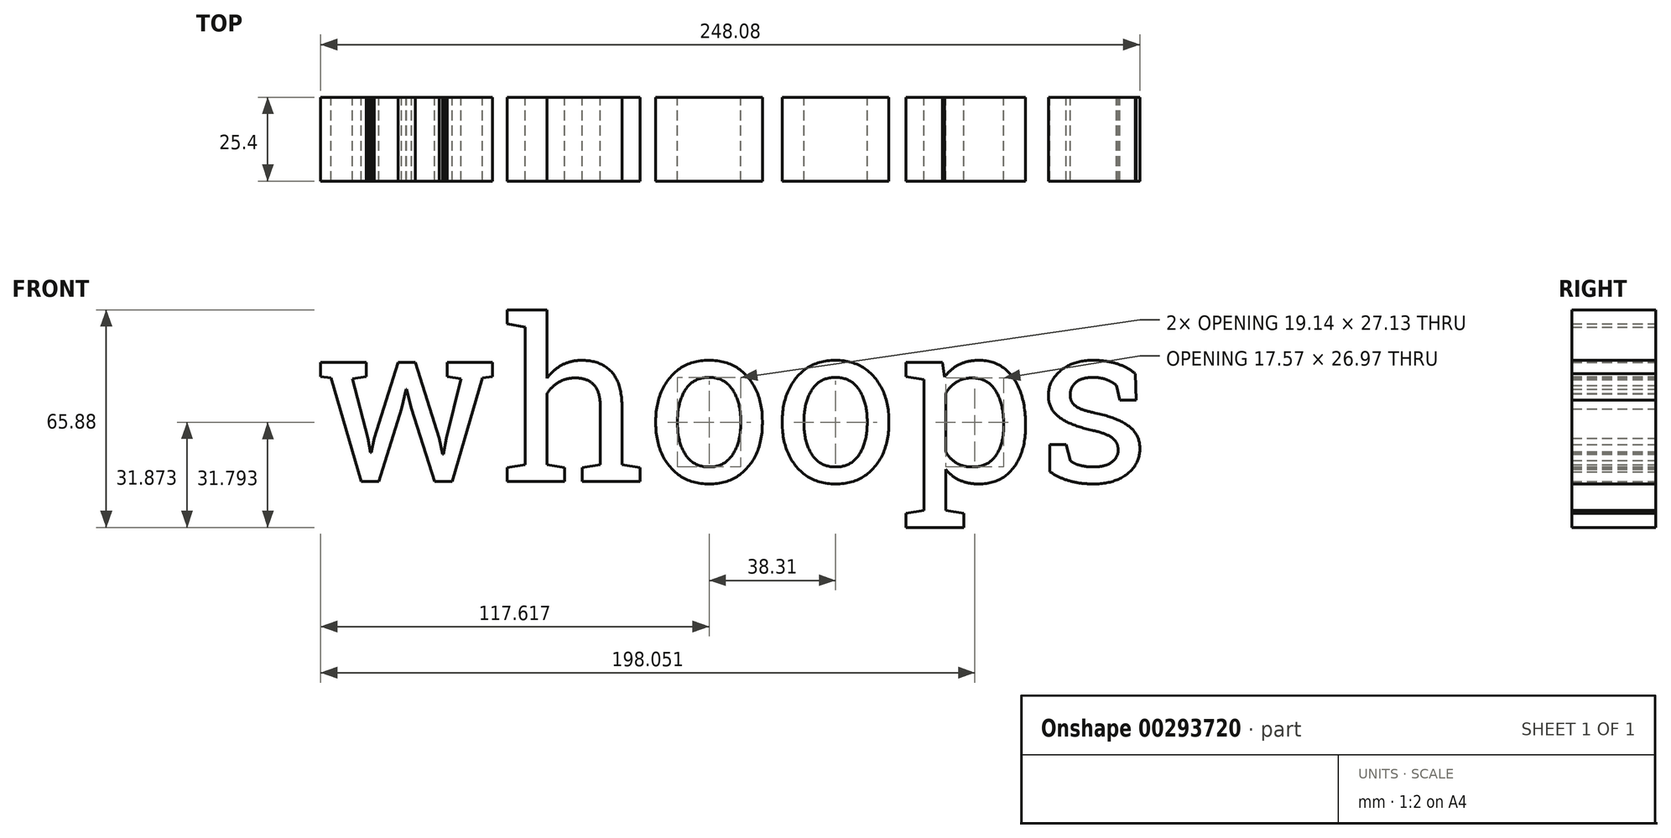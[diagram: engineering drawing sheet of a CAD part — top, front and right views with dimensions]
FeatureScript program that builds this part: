
annotation { "Feature Type Name" : "Feature", "Feature Type Description" : "" }
export const myFeature = defineFeature(function(context is Context, id is Id, definition is map)
    precondition{}
    {
        {
            var Q0;
            Q0=qCreatedBy(makeId("Front.planeOp"),FACE);
            var sketch = newSketch(context, id + "F0", { "sketchPlane" : qUnion([Q0])});
            skText(sketch, "E0", { "text": "whoops", "fontName": "RobotoSlab-Regular.ttf"});
            const initialGuessF0  = {"E0": [-0.2113, -0.0114, 1, 0, 0.04916]};
            skSetInitialGuess(sketch, initialGuessF0);
            skSolve(sketch);
        }
        {
            var Q0;
            Q0 = qSketchRegion(id + "F0", true);
            extrude(context, id + "F1", {"entities" : qUnion([Q0]), "depth" : 25.4 * mm});
        }
    });
